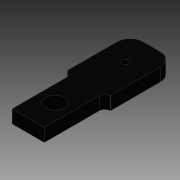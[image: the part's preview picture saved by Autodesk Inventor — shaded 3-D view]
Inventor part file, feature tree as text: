
AUTODESK INVENTOR PART (.ipt)
format: ipt  version: 2015 (Build 190159000, 159)  size: 104,960 bytes
history: native  units: in
note: dims shown in document units (in); Inventor stores cm internally (conversion verified against a paired STEP export)
features: sketch x2, extrude x1, hole x1
ambient origin geometry x8: Origin, YZ Plane, XZ Plane, XY Plane, X Axis, Y Axis, Z Axis, Center Point
bodies: Solid1 (feature_tree)
feature tree (4):
  extrude  "Extrusion1"  Depth=1.225in
  hole  "Hole2"  [1 undecoded]
  sketch  "Sketch1"  dims[d0=0.2in d1=1.225in]
  sketch  "Sketch2"  dims[d2=1.65in d3=2.4in d4=4.7in d5=0.7in d6=1.0in d7=0.5in d8=0.5in d9=0.0in d19=1.0in d20=0.25in d21=0.75in d22=0.375in d23=0.25in d24=0.5635in d25=1.0in d26=0.8108in]
note: 1 required parameter value undecoded (feature->parameter linkage not recoverable at this tier; creation-order binding heuristic only, values carry confidence <= 0.55)
